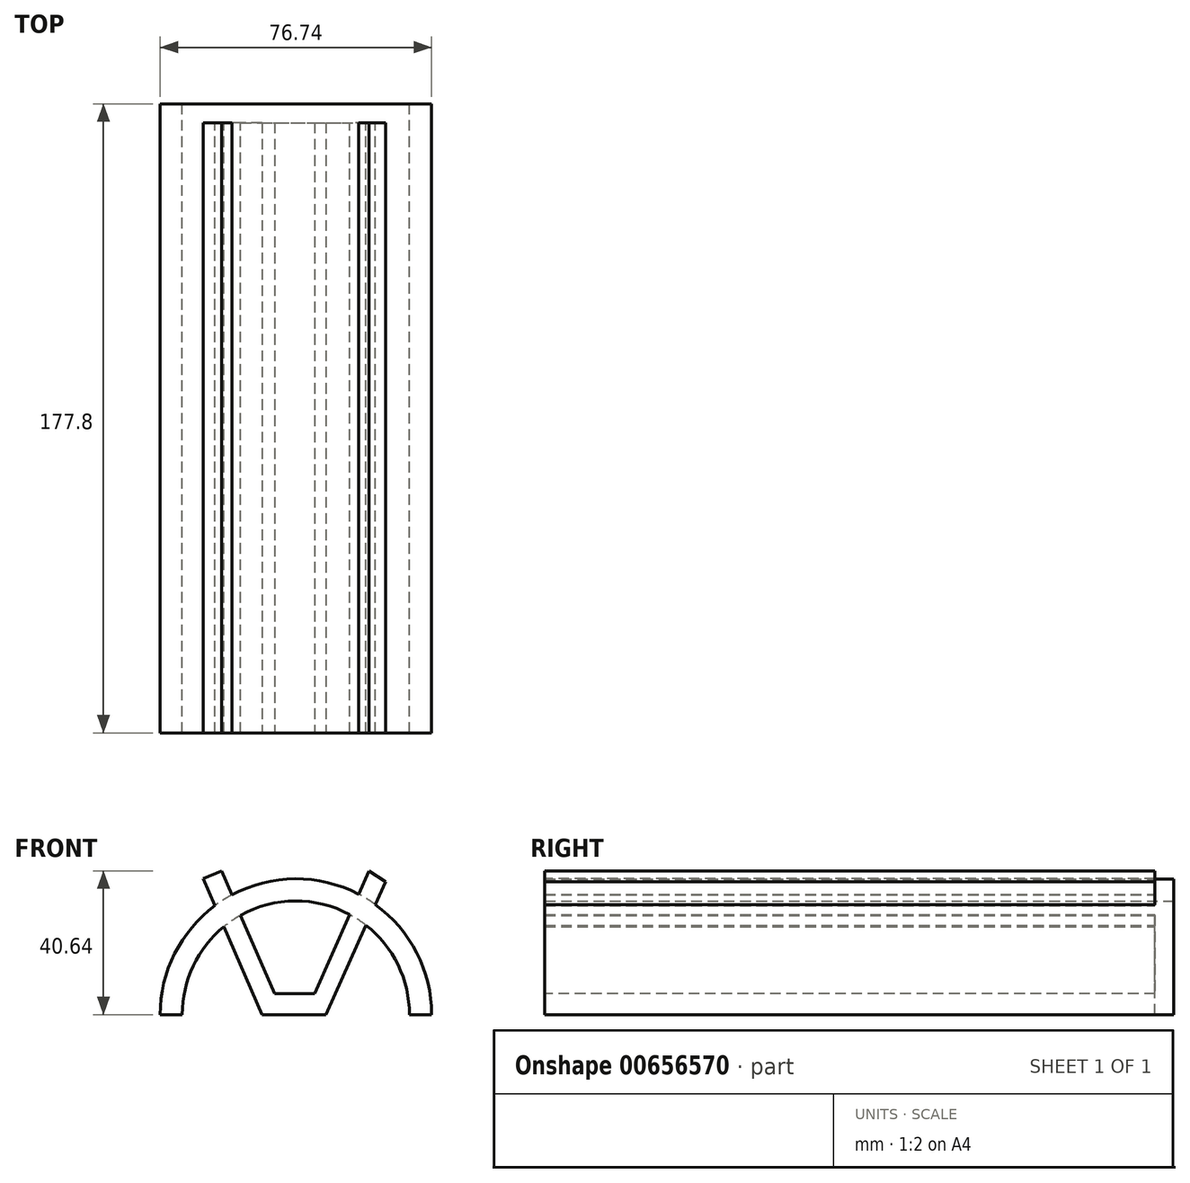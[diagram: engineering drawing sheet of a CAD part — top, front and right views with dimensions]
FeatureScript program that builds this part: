
annotation { "Feature Type Name" : "Feature", "Feature Type Description" : "" }
export const myFeature = defineFeature(function(context is Context, id is Id, definition is map)
    precondition{}
    {
        {
            var Q0;
            Q0=qCreatedBy(makeId("Front.planeOp"),FACE);
            var sketch = newSketch(context, id + "F0", { "sketchPlane" : qUnion([Q0])});
            skArc(sketch, "E0", {"start": v(0, 32.11) * mm, "mid": v(22.7, 22.7) * mm, "end": v(32.11, 0) * mm});
            skArc(sketch, "E1", {"start": v(0, 32.11) * mm, "mid": v(-22.7, 22.7) * mm, "end": v(-32.11, 0) * mm});
            skArc(sketch, "E2", {"start": v(0, 38.37) * mm, "mid": v(27.13, 27.13) * mm, "end": v(38.37, 0) * mm});
            skArc(sketch, "E3", {"start": v(0, 38.37) * mm, "mid": v(-27.13, 27.13) * mm, "end": v(-38.37, 0) * mm});
            skLineSegment(sketch, "E4", {"start": v(-38.37, 0) * mm, "end": v(-32.11, 0) * mm});
            skLineSegment(sketch, "E5", {"start": v(32.11, 0) * mm, "end": v(38.37, 0) * mm});
            skSolve(sketch);
        }
        {
            var Q0;
            Q0 = qSketchRegion(id + "F0", true);
            extrude(context, id + "F1", {"entities" : qUnion([Q0]), "depth" : 177.8 * mm, "offsetDistance" : 25.4 * mm});
        }
        {
            var Q0;
            Q0=makeQuery(id+"F1.opExtrude","CAP_FACE",FACE,{"disambiguationData":[OSD([sQuery(id+"F0.wireOp",EDGE,"E0"),sQuery(id+"F0.wireOp",EDGE,"E1"),sQuery(id+"F0.wireOp",EDGE,"E2"),sQuery(id+"F0.wireOp",EDGE,"E3"),sQuery(id+"F0.wireOp",EDGE,"E4"),sQuery(id+"F0.wireOp",EDGE,"E5")])],"isStart":false});
            var sketch = newSketch(context, id + "F2", { "sketchPlane" : qUnion([Q0])});
            skLineSegment(sketch, "E6", {"start": v(-9.59, 0) * mm, "end": v(-26.22, 38.4) * mm});
            skLineSegment(sketch, "E7", {"start": v(8.5, 0) * mm, "end": v(25.37, 37.56) * mm});
            skLineSegment(sketch, "E8", {"start": v(-26.22, 38.4) * mm, "end": v(-21.04, 40.64) * mm});
            skLineSegment(sketch, "E9", {"start": v(-21.04, 40.64) * mm, "end": v(-6, 5.9) * mm});
            skLineSegment(sketch, "E10", {"start": v(-6, 5.9) * mm, "end": v(5.26, 5.9) * mm});
            skLineSegment(sketch, "E11", {"start": v(5.26, 5.9) * mm, "end": v(20.63, 40.64) * mm});
            skLineSegment(sketch, "E12", {"start": v(20.63, 40.64) * mm, "end": v(25.37, 37.56) * mm});
            skPoint(sketch, "E13.oppositeSnap0", {"position": v(0, 38.37) * mm});
            skLineSegment(sketch, "E14", {"start": v(-9.59, 0) * mm, "end": v(0, 0) * mm});
            skLineSegment(sketch, "E15", {"start": v(8.5, 0) * mm, "end": v(0, 0) * mm});
            skSolve(sketch);
        }
        {
            var Q0;
            Q0 = qSketchRegion(id + "F2", true);
            var Q1;
            Q1 = qSketchRegion(id + "F4", true);
            extrude(context, id + "F3", {"entities" : qUnion([Q0, Q1]), "operationType" : NewBodyOperationType.ADD, "oppositeDirection" : true, "depth" : 172.47 * mm, "offsetDistance" : 25.4 * mm});
        }
    });
